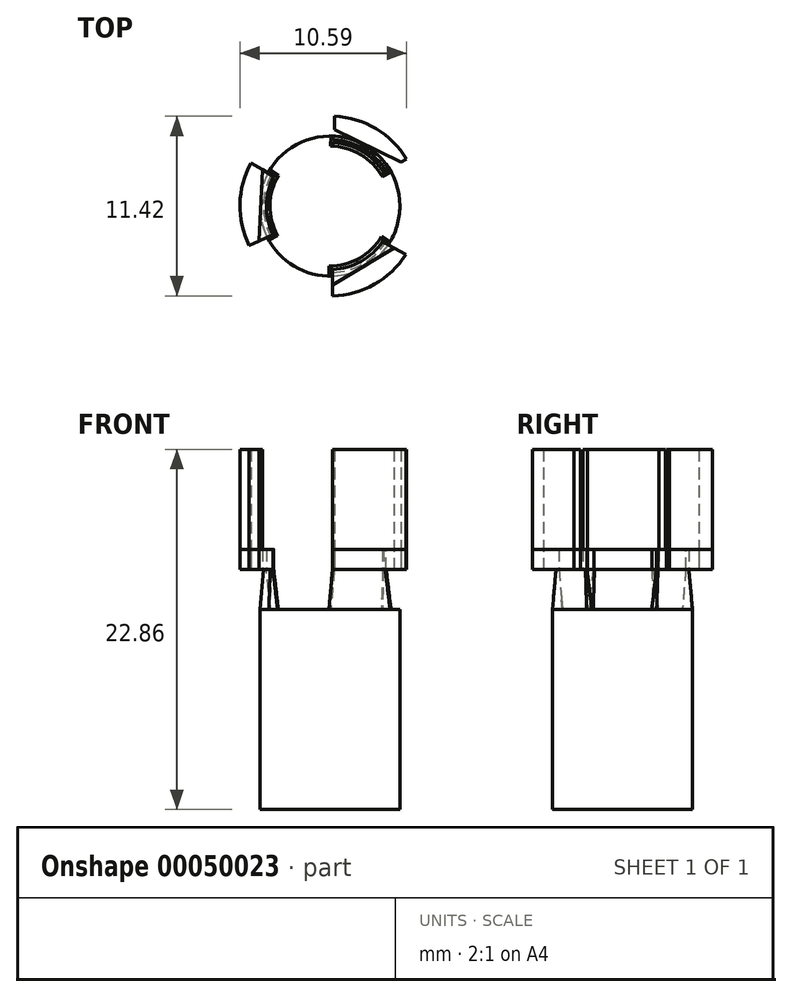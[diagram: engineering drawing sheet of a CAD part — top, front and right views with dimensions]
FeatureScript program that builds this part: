
annotation { "Feature Type Name" : "Feature", "Feature Type Description" : "" }
export const myFeature = defineFeature(function(context is Context, id is Id, definition is map)
    precondition{}
    {
        {
            var Q0;
            Q0=qCreatedBy(makeId("Top.planeOp"),FACE);
            var sketch = newSketch(context, id + "F0", { "sketchPlane" : qUnion([Q0])});
            skCircle(sketch, "E0", {"center": v(0, 0) * mm, "radius": 4.45 * mm});
            skCircle(sketch, "E1.cCircle", {"center": v(0, 0) * mm, "radius": 4.45 * mm, "construction": true});
            skLineSegment(sketch, "E1.0", {"start": v(-4.41, 2.63) * mm, "end": v(0.07, 5.13) * mm});
            skLineSegment(sketch, "E1.1", {"start": v(0.07, 5.13) * mm, "end": v(4.48, 2.5) * mm});
            skLineSegment(sketch, "E1.2", {"start": v(4.48, 2.5) * mm, "end": v(4.41, -2.63) * mm});
            skLineSegment(sketch, "E1.3", {"start": v(4.41, -2.63) * mm, "end": v(-0.07, -5.13) * mm});
            skLineSegment(sketch, "E1.4", {"start": v(-0.07, -5.13) * mm, "end": v(-4.48, -2.5) * mm});
            skLineSegment(sketch, "E1.5", {"start": v(-4.48, -2.5) * mm, "end": v(-4.41, 2.63) * mm});
            skPoint(sketch, "E1.0.midPoint", {"position": v(-2.17, 3.88) * mm});
            skLineSegment(sketch, "E2", {"start": v(-4.41, 2.63) * mm, "end": v(4.41, -2.63) * mm});
            skLineSegment(sketch, "E3", {"start": v(0.07, 5.13) * mm, "end": v(-0.07, -5.13) * mm});
            skLineSegment(sketch, "E4", {"start": v(-4.48, -2.5) * mm, "end": v(4.48, 2.5) * mm});
            skCircle(sketch, "E5", {"center": v(0, 0) * mm, "radius": 3.81 * mm});
            skSolve(sketch);
        }
        {
            var Q0;
            {var subQ1=sQuery(id+"F0.wireOp",EDGE,"E0");var subQ8=makeQuery(id+"F0.imprint","INTERSECT",VERTEX,{"derivedFrom":[subQ1,sQuery(id+"F0.wireOp",EDGE,"E1.5")]});Q0=makeQuery(id+"F0.imprint","IMPRINT",FACE,{"disambiguationData":[TD([[makeQuery(id+"F0.imprint","IMPRINT",EDGE,{"disambiguationData":[TD([[subQ8,1.0]])],"derivedFrom":subQ1}),1.0]])]});}
            var Q1;
            {var subQ1=sQuery(id+"F0.wireOp",EDGE,"E0");var subQ8=makeQuery(id+"F0.imprint","INTERSECT",VERTEX,{"derivedFrom":[subQ1,sQuery(id+"F0.wireOp",EDGE,"E1.1")]});Q1=makeQuery(id+"F0.imprint","IMPRINT",FACE,{"disambiguationData":[TD([[makeQuery(id+"F0.imprint","IMPRINT",EDGE,{"disambiguationData":[TD([[subQ8,1.0]])],"derivedFrom":subQ1}),1.0]])]});}
            var Q2;
            {var subQ1=sQuery(id+"F0.wireOp",EDGE,"E0");var subQ8=makeQuery(id+"F0.imprint","INTERSECT",VERTEX,{"derivedFrom":[subQ1,sQuery(id+"F0.wireOp",EDGE,"E1.3")]});Q2=makeQuery(id+"F0.imprint","IMPRINT",FACE,{"disambiguationData":[TD([[makeQuery(id+"F0.imprint","IMPRINT",EDGE,{"disambiguationData":[TD([[subQ8,1.0]])],"derivedFrom":subQ1}),1.0]])]});}
            extrude(context, id + "F1", {"entities" : qUnion([Q0, Q1, Q2]), "depth" : 2.54 * mm, "hasDraft" : true, "draftAngle" : 5 * degree, "draftPullDirection" : true});
        }
        {
            var Q0;
            Q0=makeQuery(id+"F1.opExtrude","CAP_FACE",FACE,{"disambiguationData":[OSD([sQuery(id+"F0.wireOp",EDGE,"E0"),sQuery(id+"F0.wireOp",EDGE,"E3"),sQuery(id+"F0.wireOp",EDGE,"E4"),sQuery(id+"F0.wireOp",EDGE,"E5")])],"isStart":false});
            var sketch = newSketch(context, id + "F2", { "sketchPlane" : qUnion([Q0])});
            skCircle(sketch, "E6", {"center": v(0, 0) * mm, "radius": 4.22 * mm});
            skCircle(sketch, "E7", {"center": v(0, 0) * mm, "radius": 4.03 * mm});
            skCircle(sketch, "E8", {"center": v(-9.57, 19.48) * mm, "radius": 4.43 * mm});
            skCircle(sketch, "E9", {"center": v(-9.57, 19.48) * mm, "radius": 4.23 * mm});
            skCircle(sketch, "E10", {"center": v(0, 0) * mm, "radius": 5.72 * mm});
            skLineSegment(sketch, "E11", {"start": v(0.28, 4.02) * mm, "end": v(0.3, 5.7) * mm});
            skPoint(sketch, "E12", {"position": v(0.28, 4.21) * mm});
            skLineSegment(sketch, "E13", {"start": v(3.4, 2.16) * mm, "end": v(4.87, 2.98) * mm});
            skPoint(sketch, "E14", {"position": v(3.57, 2.25) * mm});
            skPoint(sketch, "E15", {"position": v(3.5, -2.35) * mm});
            skPoint(sketch, "E16", {"position": v(0.17, -4.22) * mm});
            skPoint(sketch, "E17", {"position": v(-3.78, -1.88) * mm});
            skPoint(sketch, "E18", {"position": v(-3.74, 1.97) * mm});
            skLineSegment(sketch, "E19", {"start": v(3.34, -2.26) * mm, "end": v(4.82, -3.07) * mm});
            skLineSegment(sketch, "E20", {"start": v(0.17, -4.03) * mm, "end": v(0.17, -5.71) * mm});
            skLineSegment(sketch, "E21", {"start": v(-3.6, -1.8) * mm, "end": v(-5.13, -2.52) * mm});
            skLineSegment(sketch, "E22", {"start": v(-3.57, 1.87) * mm, "end": v(-5.02, 2.74) * mm});
            skLineSegment(sketch, "E23", {"start": v(0.28, 4.87) * mm, "end": v(4.53, 2.8) * mm});
            skPoint(sketch, "E23.startSnap0", {"position": v(0.29, 4.87) * mm});
            skLineSegment(sketch, "E24", {"start": v(4.53, 2.8) * mm, "end": v(4.08, -2.66) * mm});
            skLineSegment(sketch, "E25", {"start": v(4.08, -2.66) * mm, "end": v(0.17, -5.03) * mm});
            skLineSegment(sketch, "E26", {"start": v(0.17, -5.03) * mm, "end": v(-4.5, -2.22) * mm});
            skLineSegment(sketch, "E27", {"start": v(-4.5, -2.22) * mm, "end": v(-4.3, 2.3) * mm});
            skLineSegment(sketch, "E28", {"start": v(-4.3, 2.3) * mm, "end": v(0.29, 4.87) * mm});
            skSolve(sketch);
        }
        {
            var Q0;
            {var subQ0=sQuery(id+"F2.wireOp",EDGE,"E11");var subQ1=sQuery(id+"F2.wireOp",EDGE,"E6");var subQ2=makeQuery(id+"F2.imprint","INTERSECT",VERTEX,{"derivedFrom":[subQ1,subQ0]});Q0=makeQuery(id+"F2.imprint","IMPRINT",FACE,{"disambiguationData":[TD([[makeQuery(id+"F2.imprint","IMPRINT",EDGE,{"disambiguationData":[TD([[subQ2,1.0]])],"derivedFrom":subQ1}),1.0]])]});}
            var Q1;
            {var subQ1=sQuery(id+"F0.wireOp",EDGE,"E0");var subQ2=makeQuery(id+"F0.imprint","INTERSECT",VERTEX,{"derivedFrom":[subQ1,sQuery(id+"F0.wireOp",EDGE,"E1.1")]});var subQ3=makeQuery(id+"F1.opExtrude","CAP_EDGE",EDGE,{"disambiguationData":[OSD([subQ1]),TDD([makeQuery(id+"F0.imprint","IMPRINT",EDGE,{"disambiguationData":[TD([[subQ2,1.0]])],"derivedFrom":subQ1}),makeQuery(id+"F0.imprint","IMPRINT",EDGE,{"disambiguationData":[TD([[subQ2,-1.0]])],"derivedFrom":subQ1})])],"isStart":false});Q1=makeQuery(id+"F2.imprint","IMPRINT",FACE,{"disambiguationData":[TD([[makeQuery(id+"F2.imprint","IMPRINT",EDGE,{"derivedFrom":subQ3}),-1.0]])]});}
            var Q2;
            {var subQ0=sQuery(id+"F2.wireOp",EDGE,"E13");var subQ1=sQuery(id+"F2.wireOp",EDGE,"E10");var subQ2=makeQuery(id+"F2.imprint","INTERSECT",VERTEX,{"derivedFrom":[subQ1,subQ0]});Q2=makeQuery(id+"F2.imprint","IMPRINT",FACE,{"disambiguationData":[TD([[makeQuery(id+"F2.imprint","IMPRINT",EDGE,{"disambiguationData":[TD([[subQ2,-1.0]])],"derivedFrom":subQ1}),1.0]])]});}
            var Q3;
            {var subQ5=sQuery(id+"F2.wireOp",EDGE,"E25");Q3=makeQuery(id+"F2.imprint","IMPRINT",FACE,{"disambiguationData":[TD([[makeQuery(id+"F2.imprint","IMPRINT",EDGE,{"derivedFrom":subQ5}),1.0]])]});}
            var Q4;
            {var subQ5=sQuery(id+"F2.wireOp",EDGE,"E25");Q4=makeQuery(id+"F2.imprint","IMPRINT",FACE,{"disambiguationData":[TD([[makeQuery(id+"F2.imprint","IMPRINT",EDGE,{"derivedFrom":subQ5}),-1.0]])]});}
            var Q5;
            {var subQ0=sQuery(id+"F2.wireOp",EDGE,"E20");var subQ1=sQuery(id+"F2.wireOp",EDGE,"E6");var subQ2=makeQuery(id+"F2.imprint","INTERSECT",VERTEX,{"derivedFrom":[subQ1,subQ0]});Q5=makeQuery(id+"F2.imprint","IMPRINT",FACE,{"disambiguationData":[TD([[makeQuery(id+"F2.imprint","IMPRINT",EDGE,{"disambiguationData":[TD([[subQ2,-1.0]])],"derivedFrom":subQ1}),1.0]])]});}
            var Q6;
            {var subQ0=sQuery(id+"F2.wireOp",EDGE,"E22");var subQ1=sQuery(id+"F2.wireOp",EDGE,"E6");var subQ2=makeQuery(id+"F2.imprint","INTERSECT",VERTEX,{"derivedFrom":[subQ1,subQ0]});Q6=makeQuery(id+"F2.imprint","IMPRINT",FACE,{"disambiguationData":[TD([[makeQuery(id+"F2.imprint","IMPRINT",EDGE,{"disambiguationData":[TD([[subQ2,-1.0]])],"derivedFrom":subQ1}),1.0]])]});}
            var Q7;
            {var subQ5=sQuery(id+"F2.wireOp",EDGE,"E27");Q7=makeQuery(id+"F2.imprint","IMPRINT",FACE,{"disambiguationData":[TD([[makeQuery(id+"F2.imprint","IMPRINT",EDGE,{"derivedFrom":subQ5}),-1.0]])]});}
            var Q8;
            {var subQ5=sQuery(id+"F2.wireOp",EDGE,"E27");Q8=makeQuery(id+"F2.imprint","IMPRINT",FACE,{"disambiguationData":[TD([[makeQuery(id+"F2.imprint","IMPRINT",EDGE,{"derivedFrom":subQ5}),1.0]])]});}
            extrude(context, id + "F3", {"entities" : qUnion([Q0, Q1, Q2, Q3, Q4, Q5, Q6, Q7, Q8]), "depth" : 1.27 * mm});
        }
        {
            var Q0;
            {var subQ0=sQuery(id+"F2.wireOp",EDGE,"E13");var subQ1=sQuery(id+"F2.wireOp",EDGE,"E10");var subQ2=makeQuery(id+"F2.imprint","INTERSECT",VERTEX,{"derivedFrom":[subQ1,subQ0]});Q0=makeQuery(id+"F2.imprint","IMPRINT",FACE,{"disambiguationData":[TD([[makeQuery(id+"F2.imprint","IMPRINT",EDGE,{"disambiguationData":[TD([[subQ2,-1.0]])],"derivedFrom":subQ1}),1.0]])]});}
            var Q1;
            {var subQ5=sQuery(id+"F2.wireOp",EDGE,"E27");Q1=makeQuery(id+"F2.imprint","IMPRINT",FACE,{"disambiguationData":[TD([[makeQuery(id+"F2.imprint","IMPRINT",EDGE,{"derivedFrom":subQ5}),1.0]])]});}
            var Q2;
            {var subQ5=sQuery(id+"F2.wireOp",EDGE,"E25");Q2=makeQuery(id+"F2.imprint","IMPRINT",FACE,{"disambiguationData":[TD([[makeQuery(id+"F2.imprint","IMPRINT",EDGE,{"derivedFrom":subQ5}),1.0]])]});}
            extrude(context, id + "F4", {"entities" : qUnion([Q0, Q1, Q2]), "depth" : 7.62 * mm});
        }
        {
            var Q0;
            {var subQ0=sQuery(id+"F0.wireOp",EDGE,"E5");var subQ1=sQuery(id+"F0.wireOp",EDGE,"E3");var subQ2=makeQuery(id+"F0.imprint","INTERSECT",VERTEX,{"disambiguationData":[OD(1.0)],"derivedFrom":[subQ1,subQ0]});Q0=makeQuery(id+"F0.imprint","IMPRINT",FACE,{"disambiguationData":[TD([[makeQuery(id+"F0.imprint","IMPRINT",EDGE,{"disambiguationData":[TD([[subQ2,1.0]])],"derivedFrom":subQ0}),1.0]])]});}
            var Q1;
            {var subQ0=sQuery(id+"F0.wireOp",EDGE,"E5");var subQ1=sQuery(id+"F0.wireOp",EDGE,"E2");var subQ2=makeQuery(id+"F0.imprint","INTERSECT",VERTEX,{"disambiguationData":[OD(1.0)],"derivedFrom":[subQ1,subQ0]});Q1=makeQuery(id+"F0.imprint","IMPRINT",FACE,{"disambiguationData":[TD([[makeQuery(id+"F0.imprint","IMPRINT",EDGE,{"disambiguationData":[TD([[subQ2,1.0]])],"derivedFrom":subQ0}),1.0]])]});}
            var Q2;
            {var subQ0=sQuery(id+"F0.wireOp",EDGE,"E5");var subQ1=sQuery(id+"F0.wireOp",EDGE,"E2");var subQ2=makeQuery(id+"F0.imprint","INTERSECT",VERTEX,{"disambiguationData":[OD(1.0)],"derivedFrom":[subQ1,subQ0]});Q2=makeQuery(id+"F0.imprint","IMPRINT",FACE,{"disambiguationData":[TD([[makeQuery(id+"F0.imprint","IMPRINT",EDGE,{"disambiguationData":[TD([[subQ2,-1.0]])],"derivedFrom":subQ0}),1.0]])]});}
            var Q3;
            {var subQ0=sQuery(id+"F0.wireOp",EDGE,"E5");var subQ1=sQuery(id+"F0.wireOp",EDGE,"E3");var subQ2=makeQuery(id+"F0.imprint","INTERSECT",VERTEX,{"disambiguationData":[OD(0.0)],"derivedFrom":[subQ1,subQ0]});Q3=makeQuery(id+"F0.imprint","IMPRINT",FACE,{"disambiguationData":[TD([[makeQuery(id+"F0.imprint","IMPRINT",EDGE,{"disambiguationData":[TD([[subQ2,1.0]])],"derivedFrom":subQ0}),1.0]])]});}
            var Q4;
            {var subQ0=sQuery(id+"F0.wireOp",EDGE,"E5");var subQ1=sQuery(id+"F0.wireOp",EDGE,"E2");var subQ2=makeQuery(id+"F0.imprint","INTERSECT",VERTEX,{"disambiguationData":[OD(0.0)],"derivedFrom":[subQ1,subQ0]});Q4=makeQuery(id+"F0.imprint","IMPRINT",FACE,{"disambiguationData":[TD([[makeQuery(id+"F0.imprint","IMPRINT",EDGE,{"disambiguationData":[TD([[subQ2,1.0]])],"derivedFrom":subQ0}),1.0]])]});}
            var Q5;
            {var subQ0=sQuery(id+"F0.wireOp",EDGE,"E5");var subQ1=sQuery(id+"F0.wireOp",EDGE,"E2");var subQ2=makeQuery(id+"F0.imprint","INTERSECT",VERTEX,{"disambiguationData":[OD(0.0)],"derivedFrom":[subQ1,subQ0]});Q5=makeQuery(id+"F0.imprint","IMPRINT",FACE,{"disambiguationData":[TD([[makeQuery(id+"F0.imprint","IMPRINT",EDGE,{"disambiguationData":[TD([[subQ2,-1.0]])],"derivedFrom":subQ0}),1.0]])]});}
            var Q6;
            {var subQ1=sQuery(id+"F0.wireOp",EDGE,"E0");var subQ8=makeQuery(id+"F0.imprint","INTERSECT",VERTEX,{"derivedFrom":[subQ1,sQuery(id+"F0.wireOp",EDGE,"E1.5")]});Q6=makeQuery(id+"F0.imprint","IMPRINT",FACE,{"disambiguationData":[TD([[makeQuery(id+"F0.imprint","IMPRINT",EDGE,{"disambiguationData":[TD([[subQ8,1.0]])],"derivedFrom":subQ1}),1.0]])]});}
            var Q7;
            {var subQ1=sQuery(id+"F0.wireOp",EDGE,"E0");var subQ5=makeQuery(id+"F0.imprint","INTERSECT",VERTEX,{"derivedFrom":[subQ1,sQuery(id+"F0.wireOp",EDGE,"E1.4")]});Q7=makeQuery(id+"F0.imprint","IMPRINT",FACE,{"disambiguationData":[TD([[makeQuery(id+"F0.imprint","IMPRINT",EDGE,{"disambiguationData":[TD([[subQ5,1.0]])],"derivedFrom":subQ1}),1.0]])]});}
            var Q8;
            {var subQ1=sQuery(id+"F0.wireOp",EDGE,"E0");var subQ8=makeQuery(id+"F0.imprint","INTERSECT",VERTEX,{"derivedFrom":[subQ1,sQuery(id+"F0.wireOp",EDGE,"E1.3")]});Q8=makeQuery(id+"F0.imprint","IMPRINT",FACE,{"disambiguationData":[TD([[makeQuery(id+"F0.imprint","IMPRINT",EDGE,{"disambiguationData":[TD([[subQ8,1.0]])],"derivedFrom":subQ1}),1.0]])]});}
            var Q9;
            {var subQ1=sQuery(id+"F0.wireOp",EDGE,"E0");var subQ8=makeQuery(id+"F0.imprint","INTERSECT",VERTEX,{"derivedFrom":[subQ1,sQuery(id+"F0.wireOp",EDGE,"E1.2")]});Q9=makeQuery(id+"F0.imprint","IMPRINT",FACE,{"disambiguationData":[TD([[makeQuery(id+"F0.imprint","IMPRINT",EDGE,{"disambiguationData":[TD([[subQ8,1.0]])],"derivedFrom":subQ1}),1.0]])]});}
            var Q10;
            {var subQ1=sQuery(id+"F0.wireOp",EDGE,"E0");var subQ8=makeQuery(id+"F0.imprint","INTERSECT",VERTEX,{"derivedFrom":[subQ1,sQuery(id+"F0.wireOp",EDGE,"E1.0")]});Q10=makeQuery(id+"F0.imprint","IMPRINT",FACE,{"disambiguationData":[TD([[makeQuery(id+"F0.imprint","IMPRINT",EDGE,{"disambiguationData":[TD([[subQ8,1.0]])],"derivedFrom":subQ1}),1.0]])]});}
            var Q11;
            {var subQ1=sQuery(id+"F0.wireOp",EDGE,"E0");var subQ8=makeQuery(id+"F0.imprint","INTERSECT",VERTEX,{"derivedFrom":[subQ1,sQuery(id+"F0.wireOp",EDGE,"E1.1")]});Q11=makeQuery(id+"F0.imprint","IMPRINT",FACE,{"disambiguationData":[TD([[makeQuery(id+"F0.imprint","IMPRINT",EDGE,{"disambiguationData":[TD([[subQ8,1.0]])],"derivedFrom":subQ1}),1.0]])]});}
            extrude(context, id + "F5", {"entities" : qUnion([Q0, Q1, Q2, Q3, Q4, Q5, Q6, Q7, Q8, Q9, Q10, Q11]), "oppositeDirection" : true, "depth" : 12.7 * mm});
        }
    });
